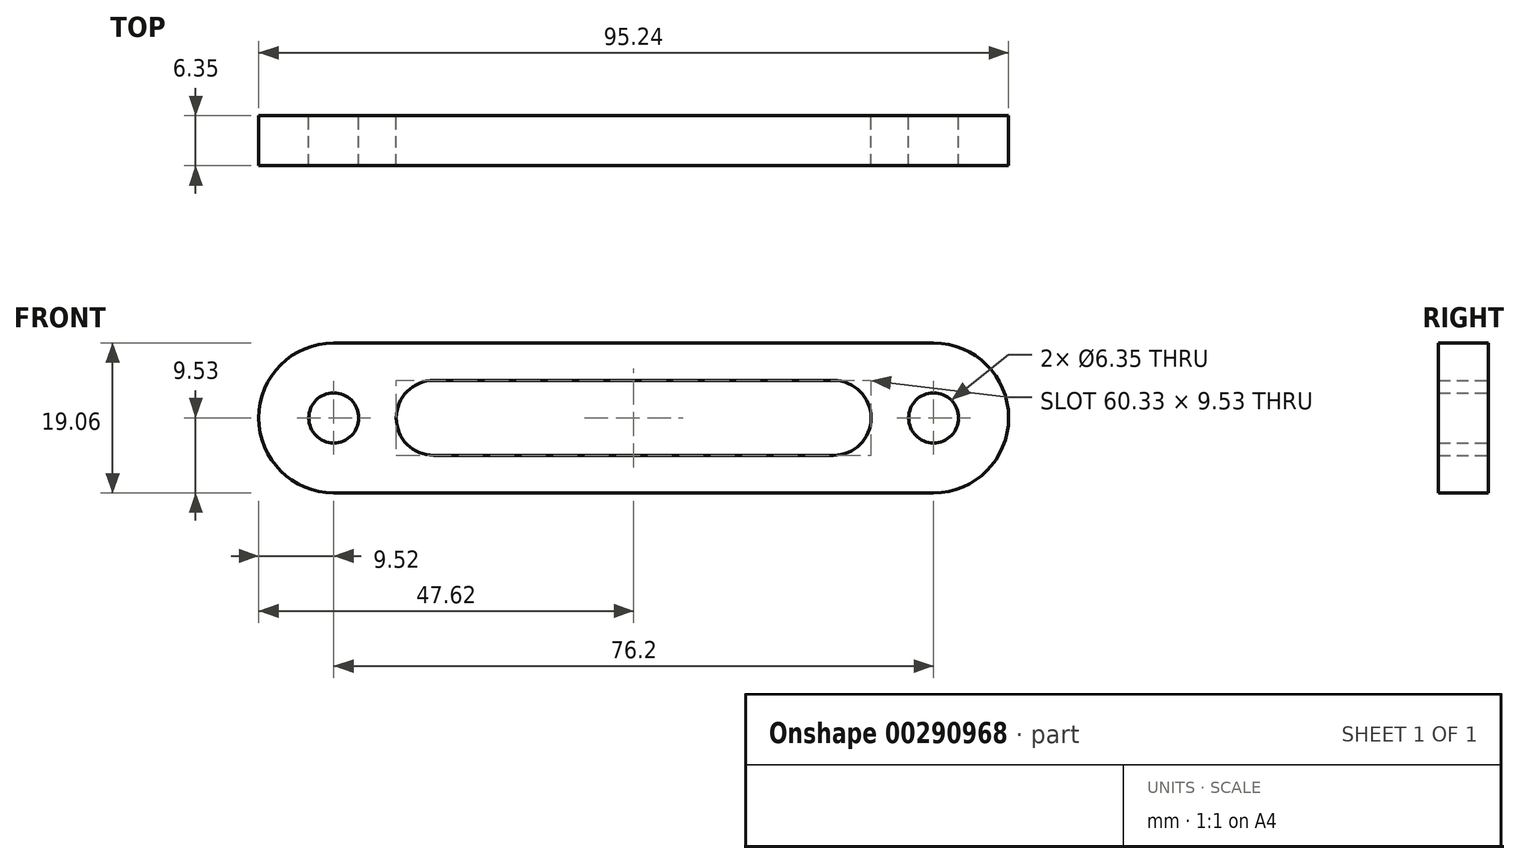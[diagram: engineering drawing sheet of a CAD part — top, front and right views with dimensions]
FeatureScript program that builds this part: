
annotation { "Feature Type Name" : "Feature", "Feature Type Description" : "" }
export const myFeature = defineFeature(function(context is Context, id is Id, definition is map)
    precondition{}
    {
        {
            var Q0;
            Q0=qCreatedBy(makeId("Front.planeOp"),FACE);
            var sketch = newSketch(context, id + "F0", { "sketchPlane" : qUnion([Q0])});
            skLineSegment(sketch, "E0.bottom", {"start": v(-25.4, 4.76) * mm, "end": v(25.4, 4.76) * mm});
            skLineSegment(sketch, "E0.top", {"start": v(-25.4, -4.76) * mm, "end": v(25.4, -4.76) * mm});
            skPoint(sketch, "E0.middle", {"position": v(0, 0) * mm});
            skLineSegment(sketch, "E1.bottom", {"start": v(-38.1, 9.52) * mm, "end": v(38.1, 9.52) * mm});
            skLineSegment(sketch, "E1.top", {"start": v(-38.1, -9.52) * mm, "end": v(38.1, -9.52) * mm});
            skCircle(sketch, "E2", {"center": v(-38.1, 0) * mm, "radius": 3.18 * mm});
            skCircle(sketch, "E3", {"center": v(38.1, 0) * mm, "radius": 3.18 * mm});
            skArc(sketch, "E4", {"start": v(-25.4, 4.76) * mm, "mid": v(-30.16, 0) * mm, "end": v(-25.4, -4.76) * mm});
            skArc(sketch, "E5", {"start": v(25.4, -4.76) * mm, "mid": v(30.16, 0) * mm, "end": v(25.4, 4.76) * mm});
            skArc(sketch, "E6", {"start": v(-38.1, 9.52) * mm, "mid": v(-47.62, 0) * mm, "end": v(-38.1, -9.52) * mm});
            skArc(sketch, "E7", {"start": v(38.1, -9.52) * mm, "mid": v(47.63, 0) * mm, "end": v(38.1, 9.52) * mm});
            skSolve(sketch);
        }
        {
            var Q0;
            Q0=makeQuery(id+"F0.imprint","IMPRINT",FACE,{"disambiguationData":[TD([[makeQuery(id+"F0.imprint","IMPRINT",EDGE,{"derivedFrom":sQuery(id+"F0.wireOp",EDGE,"E0.bottom")}),1.0]])]});
            extrude(context, id + "F1", {"entities" : qUnion([Q0]), "depth" : 6.35 * mm});
        }
    });
